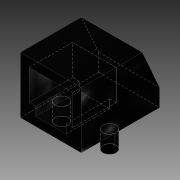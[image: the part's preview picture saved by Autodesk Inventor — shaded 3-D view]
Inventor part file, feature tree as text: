
AUTODESK INVENTOR PART (.ipt)
format: ipt  version: 2014 (Build 180170000, 170)  size: 134,144 bytes
history: native  units: mm
features: extrude x3, sketch x3
ambient origin geometry x8: Origin, YZ Plane, XZ Plane, XY Plane, X Axis, Y Axis, Z Axis, Center Point
bodies: Solid1 (feature_tree)
feature tree (6):
  extrude  "Extrusion1"  Depth=18.0mm
  extrude  "Extrusion2"  TaperAngle=0.0deg  [1 undecoded]
  extrude  "Extrusion3"  Depth=14.0mm
  sketch  "Sketch1"  dims[d0=13.0mm d1=18.0mm]
  sketch  "Sketch2"  dims[d2=9.0mm d3=0.0mm]
  sketch  "Sketch3"  dims[d4=4.0mm d5=14.0mm d6=14.0mm d7=0.0mm d8=10.0mm d9=7.0mm d10=2.0mm d11=2.0mm d12=2.0mm d13=7.0mm d14=2.0mm d15=0.0mm d16=3.5mm d17=10.0mm d18=0.0mm d19=3.0mm d20=1.5mm d21=1.5mm d22=8.0mm d23=8.0mm d24=4.0mm d25=0.0mm]
note: 1 required parameter value undecoded (feature->parameter linkage not recoverable at this tier; creation-order binding heuristic only, values carry confidence <= 0.55)
